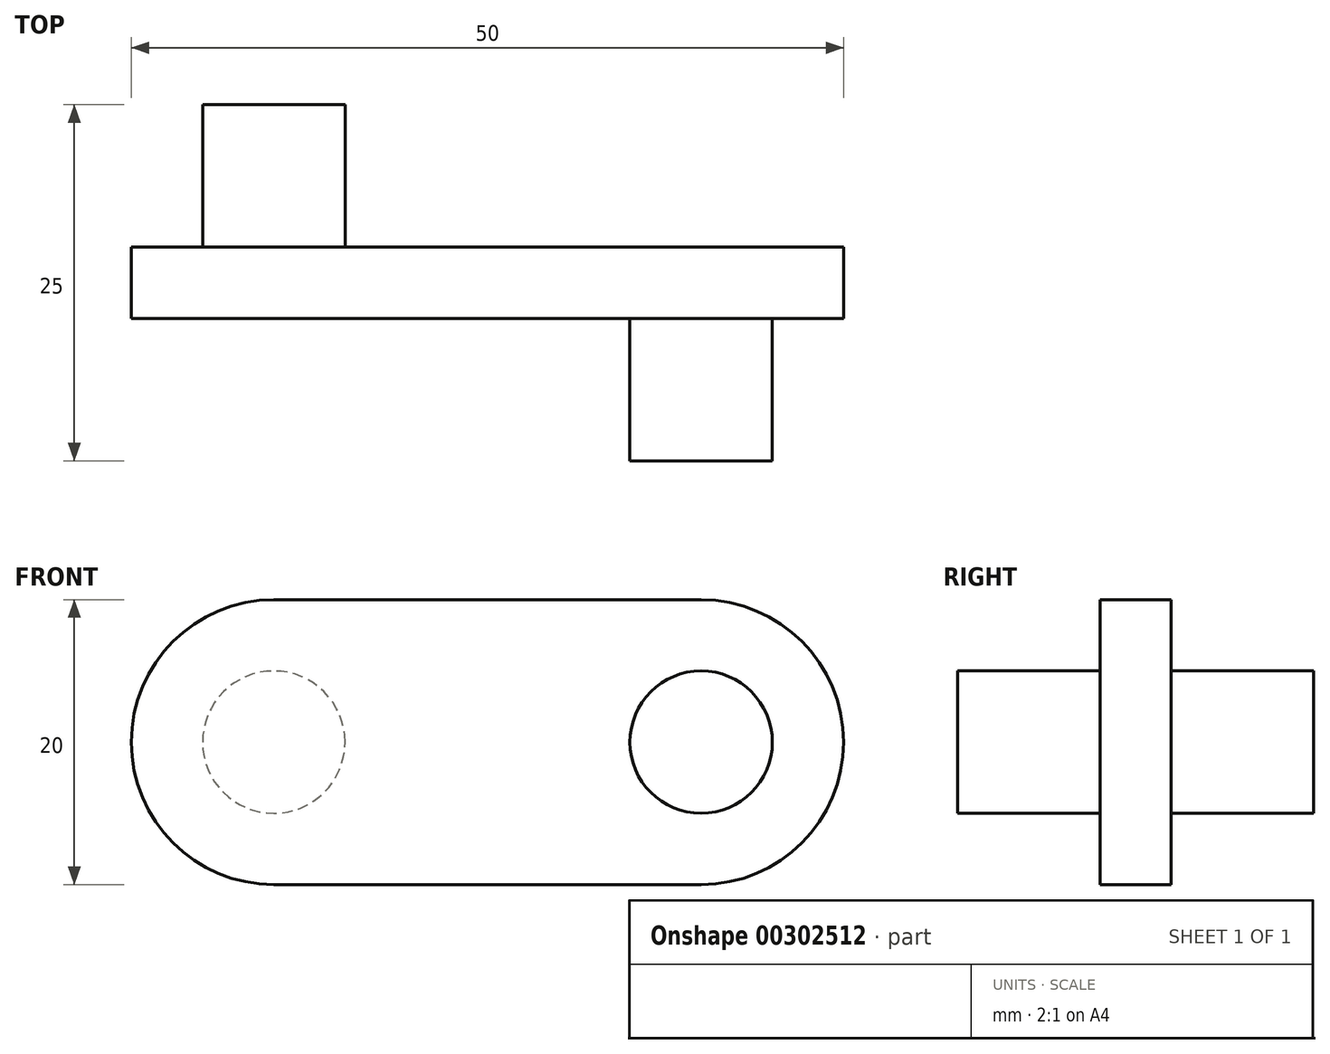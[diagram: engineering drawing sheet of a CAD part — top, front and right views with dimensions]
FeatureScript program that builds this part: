
annotation { "Feature Type Name" : "Feature", "Feature Type Description" : "" }
export const myFeature = defineFeature(function(context is Context, id is Id, definition is map)
    precondition{}
    {
        {
            var Q0;
            Q0=qCreatedBy(makeId("Front.planeOp"),FACE);
            var sketch = newSketch(context, id + "F0", { "sketchPlane" : qUnion([Q0])});
            skLineSegment(sketch, "E0", {"start": v(0, 0) * mm, "end": v(30, 0) * mm});
            skLineSegment(sketch, "E1", {"start": v(0, 20) * mm, "end": v(30, 20) * mm});
            skArc(sketch, "E2", {"start": v(0, 20) * mm, "mid": v(-10, 10) * mm, "end": v(0, 0) * mm});
            skArc(sketch, "E3", {"start": v(30, 0) * mm, "mid": v(40, 10) * mm, "end": v(30, 20) * mm});
            skCircle(sketch, "E4", {"center": v(0, 10) * mm, "radius": 5 * mm});
            skCircle(sketch, "E5", {"center": v(30, 10) * mm, "radius": 5 * mm});
            skSolve(sketch);
        }
        {
            var Q0;
            Q0=makeQuery(id+"F0.imprint","IMPRINT",FACE,{"disambiguationData":[TD([[makeQuery(id+"F0.imprint","IMPRINT",EDGE,{"derivedFrom":sQuery(id+"F0.wireOp",EDGE,"E0")}),1.0]])]});
            extrude(context, id + "F1", {"entities" : qUnion([Q0]), "depth" : 5 * mm, "symmetric" : true});
        }
        {
            var Q0;
            Q0=qCreatedBy(makeId("Front.planeOp"),FACE);
            var sketch = newSketch(context, id + "F2", { "sketchPlane" : qUnion([Q0])});
            skCircle(sketch, "E6", {"center": v(0, 10) * mm, "radius": 5 * mm});
            skCircle(sketch, "E7", {"center": v(30, 10) * mm, "radius": 5 * mm});
            skSolve(sketch);
        }
        {
            var Q0;
            Q0=makeQuery(id+"F2.imprint","IMPRINT",FACE,{"disambiguationData":[TD([[makeQuery(id+"F2.imprint","IMPRINT",EDGE,{"derivedFrom":sQuery(id+"F2.wireOp",EDGE,"E6")}),1.0]])]});
            extrude(context, id + "F3", {"entities" : qUnion([Q0]), "operationType" : NewBodyOperationType.ADD, "oppositeDirection" : true, "depth" : 12.5 * mm, "hasSecondDirection" : true, "secondDirectionOppositeDirection" : false, "secondDirectionDepth" : 2.5 * mm});
        }
        {
            var Q0;
            Q0=makeQuery(id+"F2.imprint","IMPRINT",FACE,{"disambiguationData":[TD([[makeQuery(id+"F2.imprint","IMPRINT",EDGE,{"derivedFrom":sQuery(id+"F2.wireOp",EDGE,"E7")}),1.0]])]});
            extrude(context, id + "F4", {"entities" : qUnion([Q0]), "operationType" : NewBodyOperationType.ADD, "depth" : 12.5 * mm, "hasSecondDirection" : true, "secondDirectionOppositeDirection" : true, "secondDirectionDepth" : 2.5 * mm});
        }
    });
